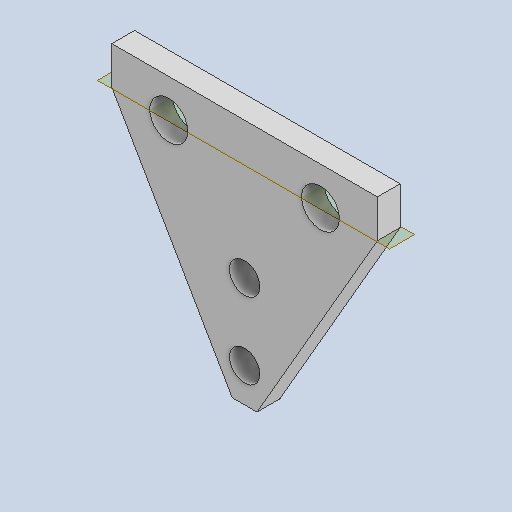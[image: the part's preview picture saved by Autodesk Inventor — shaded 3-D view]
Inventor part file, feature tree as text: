
AUTODESK INVENTOR PART (.ipt)
format: ipt  version: 2022 (Build 260153000, 153)  size: 114,176 bytes
history: native  units: in
note: dims shown in document units (in); Inventor stores cm internally (conversion verified against a paired STEP export)
features: other x3, plane x3, sketch x1
ambient origin geometry x8: Origin, YZ Plane, XZ Plane, XY Plane, X Axis, Y Axis, Z Axis, Center Point
bodies: Solid1 (feature_tree)
feature tree (7):
  other  "Load Cell Connector to Extrusion Bar.ipt"
  other  "Solid1::Load Cell Connector to Extrusion Bar.ipt"
  other  "TaggingFeature1"
  sketch  "Sketch1"  dims[d0=0.3937in]
  plane  "Work Plane1"
  plane  "Work Plane4"
  plane  "Work Plane5"
